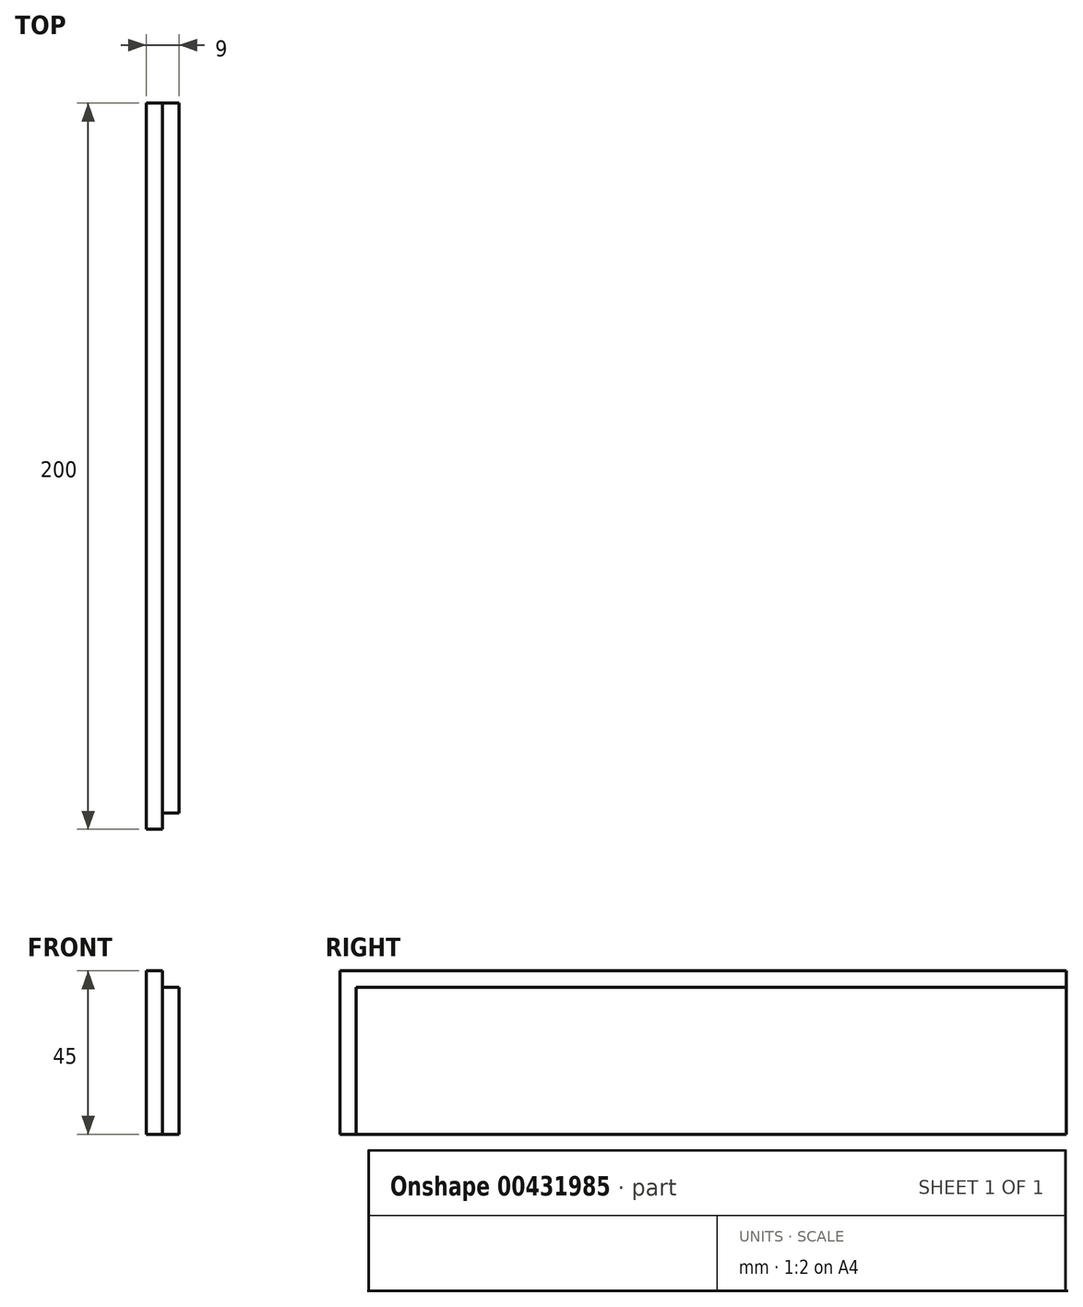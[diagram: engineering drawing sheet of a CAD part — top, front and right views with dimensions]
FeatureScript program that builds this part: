
annotation { "Feature Type Name" : "Feature", "Feature Type Description" : "" }
export const myFeature = defineFeature(function(context is Context, id is Id, definition is map)
    precondition{}
    {
        {
            var Q0;
            Q0=qCreatedBy(makeId("Right.planeOp"),FACE);
            var sketch = newSketch(context, id + "F0", { "sketchPlane" : qUnion([Q0])});
            skLineSegment(sketch, "E0.bottom", {"start": v(100, 22.5) * mm, "end": v(-100, 22.5) * mm});
            skLineSegment(sketch, "E0.top", {"start": v(100, -22.5) * mm, "end": v(-100, -22.5) * mm});
            skLineSegment(sketch, "E0.left", {"start": v(100, 22.5) * mm, "end": v(100, -22.5) * mm});
            skLineSegment(sketch, "E0.right", {"start": v(-100, 22.5) * mm, "end": v(-100, -22.5) * mm});
            skPoint(sketch, "E0.middle", {"position": v(0, 0) * mm});
            skSolve(sketch);
        }
        {
            var Q0;
            Q0=qSketchRegion(id+"F0",true);
            extrude(context, id + "F1", {"entities" : qUnion([Q0]), "depth" : 9 * mm, "offsetDistance" : 25 * mm});
        }
        {
            var Q0;
            Q0=makeQuery(id+"F1.opExtrude","SWEPT_FACE",FACE,{"disambiguationData":[OSD([sQuery(id+"F0.wireOp",EDGE,"E0.right")])]});
            var sketch = newSketch(context, id + "F2", { "sketchPlane" : qUnion([Q0])});
            skLineSegment(sketch, "E1.bottom", {"start": v(9, 22.5) * mm, "end": v(4.5, 22.5) * mm});
            skLineSegment(sketch, "E1.top", {"start": v(9, 18) * mm, "end": v(4.5, 18) * mm});
            skLineSegment(sketch, "E1.left", {"start": v(9, 22.5) * mm, "end": v(9, 18) * mm});
            skLineSegment(sketch, "E1.right", {"start": v(4.5, 22.5) * mm, "end": v(4.5, 18) * mm});
            skSolve(sketch);
        }
        {
            var Q0;
            Q0=qSketchRegion(id+"F2",true);
            extrude(context, id + "F3", {"entities" : qUnion([Q0]), "operationType" : NewBodyOperationType.REMOVE, "endBound" : BoundingType.THROUGH_ALL, "oppositeDirection" : true, "depth" : 25 * mm, "offsetDistance" : 25 * mm});
        }
        {
            var Q0;
            Q0=makeQuery(id+"F3.boolean.opBoolean","COPY",FACE,{"derivedFrom":makeQuery(id+"F3.opExtrude","SWEPT_FACE",FACE,{"disambiguationData":[OSD([sQuery(id+"F2.wireOp",EDGE,"E1.top")])]})});
            var sketch = newSketch(context, id + "F4", { "sketchPlane" : qUnion([Q0])});
            skLineSegment(sketch, "E2.bottom", {"start": v(9, -100) * mm, "end": v(4.5, -100) * mm});
            skLineSegment(sketch, "E2.top", {"start": v(9, -95.5) * mm, "end": v(4.5, -95.5) * mm});
            skLineSegment(sketch, "E2.left", {"start": v(9, -100) * mm, "end": v(9, -95.5) * mm});
            skLineSegment(sketch, "E2.right", {"start": v(4.5, -100) * mm, "end": v(4.5, -95.5) * mm});
            skSolve(sketch);
        }
        {
            var Q0;
            Q0=qSketchRegion(id+"F4",true);
            extrude(context, id + "F5", {"entities" : qUnion([Q0]), "operationType" : NewBodyOperationType.REMOVE, "endBound" : BoundingType.UP_TO_NEXT, "oppositeDirection" : true, "depth" : 25 * mm, "offsetDistance" : 25 * mm});
        }
    });
